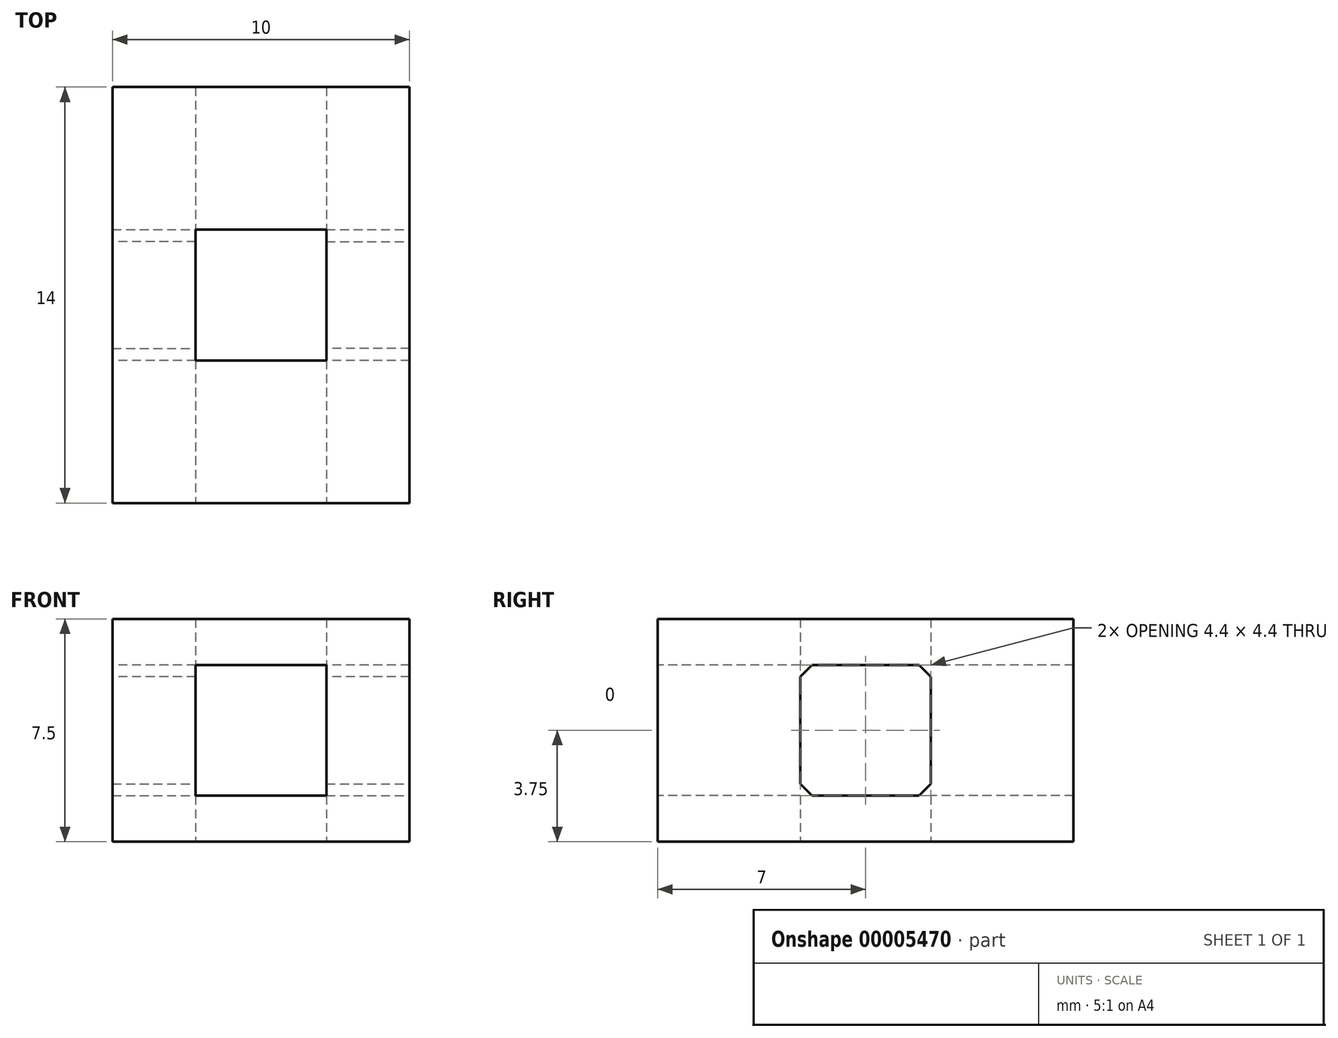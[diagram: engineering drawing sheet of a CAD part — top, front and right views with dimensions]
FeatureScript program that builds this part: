
annotation { "Feature Type Name" : "Feature", "Feature Type Description" : "" }
export const myFeature = defineFeature(function(context is Context, id is Id, definition is map)
    precondition{}
    {
        {
            var Q0;
            Q0=qCreatedBy(makeId("Top.planeOp"),FACE);
            var sketch = newSketch(context, id + "F0", { "sketchPlane" : qUnion([Q0])});
            skLineSegment(sketch, "E0.rect.bottom", {"start": v(5, 7) * mm, "end": v(-5, 7) * mm});
            skLineSegment(sketch, "E0.rect.top", {"start": v(5, -7) * mm, "end": v(-5, -7) * mm});
            skLineSegment(sketch, "E0.rect.left", {"start": v(5, 7) * mm, "end": v(5, -7) * mm});
            skLineSegment(sketch, "E0.rect.right", {"start": v(-5, 7) * mm, "end": v(-5, -7) * mm});
            skPoint(sketch, "E0.rect.middle", {"position": v(0, 0) * mm});
            skLineSegment(sketch, "E1.rect.bottom", {"start": v(2.2, 2.2) * mm, "end": v(-2.2, 2.2) * mm});
            skLineSegment(sketch, "E1.rect.top", {"start": v(2.2, -2.2) * mm, "end": v(-2.2, -2.2) * mm});
            skLineSegment(sketch, "E1.rect.left", {"start": v(2.2, 2.2) * mm, "end": v(2.2, -2.2) * mm});
            skLineSegment(sketch, "E1.rect.right", {"start": v(-2.2, 2.2) * mm, "end": v(-2.2, -2.2) * mm});
            skSolve(sketch);
        }
        {
            var Q0;
            Q0=makeQuery(id+"F0.imprint","IMPRINT",FACE,{"disambiguationData":[TD([[makeQuery(id+"F0.imprint","IMPRINT",EDGE,{"derivedFrom":sQuery(id+"F0.wireOp",EDGE,"E0.rect.bottom")}),1.0]])]});
            extrude(context, id + "F1", {"entities" : qUnion([Q0]), "depth" : 7.5 * mm});
        }
        {
            var Q0;
            Q0=makeQuery(id+"F1.opExtrude","SWEPT_FACE",FACE,{"disambiguationData":[OSD([sQuery(id+"F0.wireOp",EDGE,"E0.rect.right")])]});
            var sketch = newSketch(context, id + "F2", { "sketchPlane" : qUnion([Q0])});
            skLineSegment(sketch, "E2.rect.bottom", {"start": v(-2.2, 5.95) * mm, "end": v(2.2, 5.95) * mm});
            skLineSegment(sketch, "E2.rect.top", {"start": v(-2.2, 1.55) * mm, "end": v(2.2, 1.55) * mm});
            skLineSegment(sketch, "E2.rect.left", {"start": v(-2.2, 5.95) * mm, "end": v(-2.2, 1.55) * mm});
            skLineSegment(sketch, "E2.rect.right", {"start": v(2.2, 5.95) * mm, "end": v(2.2, 1.55) * mm});
            skPoint(sketch, "E2.rect.middle", {"position": v(0, 3.75) * mm});
            skPoint(sketch, "E3", {"position": v(-7, 3.75) * mm});
            skSolve(sketch);
        }
        {
            var Q0;
            Q0=makeQuery(id+"F2.imprint","IMPRINT",FACE,{"disambiguationData":[TD([[makeQuery(id+"F2.imprint","IMPRINT",EDGE,{"derivedFrom":sQuery(id+"F2.wireOp",EDGE,"E2.rect.bottom")}),-1.0]])]});
            extrude(context, id + "F3", {"entities" : qUnion([Q0]), "operationType" : NewBodyOperationType.REMOVE, "endBound" : BoundingType.THROUGH_ALL, "oppositeDirection" : true, "depth" : 25 * mm});
        }
        {
            var Q0;
            Q0=makeQuery(id+"F1.opExtrude","SWEPT_FACE",FACE,{"disambiguationData":[OSD([sQuery(id+"F0.wireOp",EDGE,"E0.rect.top")])]});
            var sketch = newSketch(context, id + "F4", { "sketchPlane" : qUnion([Q0])});
            skLineSegment(sketch, "E4.rect.bottom", {"start": v(2.2, 5.95) * mm, "end": v(-2.2, 5.95) * mm});
            skLineSegment(sketch, "E4.rect.top", {"start": v(2.2, 1.55) * mm, "end": v(-2.2, 1.55) * mm});
            skLineSegment(sketch, "E4.rect.left", {"start": v(2.2, 5.95) * mm, "end": v(2.2, 1.55) * mm});
            skLineSegment(sketch, "E4.rect.right", {"start": v(-2.2, 5.95) * mm, "end": v(-2.2, 1.55) * mm});
            skPoint(sketch, "E4.rect.middle", {"position": v(0, 3.75) * mm});
            skPoint(sketch, "E5", {"position": v(-5, 3.75) * mm});
            skSolve(sketch);
        }
        {
            var Q0;
            Q0=makeQuery(id+"F4.imprint","IMPRINT",FACE,{"disambiguationData":[TD([[makeQuery(id+"F4.imprint","IMPRINT",EDGE,{"derivedFrom":sQuery(id+"F4.wireOp",EDGE,"E4.rect.bottom")}),1.0]])]});
            extrude(context, id + "F5", {"entities" : qUnion([Q0]), "operationType" : NewBodyOperationType.REMOVE, "endBound" : BoundingType.THROUGH_ALL, "oppositeDirection" : true, "depth" : 25 * mm});
        }
        {
            var Q0;
            {var subQ0=sQuery(id+"F2.wireOp",EDGE,"E2.rect.top");var subQ1=sQuery(id+"F2.wireOp",EDGE,"E2.rect.left");Q0=makeQuery(id+"F3.boolean.opBoolean","COPY",EDGE,{"disambiguationData":[TD([makeQuery(id+"F1.opExtrude","SWEPT_FACE",FACE,{"disambiguationData":[OSD([sQuery(id+"F0.wireOp",EDGE,"E0.rect.left")])]})])],"derivedFrom":makeQuery(id+"F3.opExtrude","SWEPT_EDGE",EDGE,{"disambiguationData":[OSD([subQ0,subQ1])]})});}
            var Q1;
            {var subQ0=sQuery(id+"F2.wireOp",EDGE,"E2.rect.bottom");var subQ1=sQuery(id+"F2.wireOp",EDGE,"E2.rect.left");Q1=makeQuery(id+"F3.boolean.opBoolean","COPY",EDGE,{"disambiguationData":[TD([makeQuery(id+"F1.opExtrude","SWEPT_FACE",FACE,{"disambiguationData":[OSD([sQuery(id+"F0.wireOp",EDGE,"E0.rect.left")])]})])],"derivedFrom":makeQuery(id+"F3.opExtrude","SWEPT_EDGE",EDGE,{"disambiguationData":[OSD([subQ0,subQ1])]})});}
            var Q2;
            {var subQ0=sQuery(id+"F2.wireOp",EDGE,"E2.rect.bottom");var subQ1=sQuery(id+"F2.wireOp",EDGE,"E2.rect.right");Q2=makeQuery(id+"F3.boolean.opBoolean","COPY",EDGE,{"disambiguationData":[TD([makeQuery(id+"F1.opExtrude","SWEPT_FACE",FACE,{"disambiguationData":[OSD([sQuery(id+"F0.wireOp",EDGE,"E0.rect.left")])]})])],"derivedFrom":makeQuery(id+"F3.opExtrude","SWEPT_EDGE",EDGE,{"disambiguationData":[OSD([subQ0,subQ1])]})});}
            var Q3;
            {var subQ0=sQuery(id+"F2.wireOp",EDGE,"E2.rect.top");var subQ1=sQuery(id+"F2.wireOp",EDGE,"E2.rect.right");Q3=makeQuery(id+"F3.boolean.opBoolean","COPY",EDGE,{"disambiguationData":[TD([makeQuery(id+"F1.opExtrude","SWEPT_FACE",FACE,{"disambiguationData":[OSD([sQuery(id+"F0.wireOp",EDGE,"E0.rect.left")])]})])],"derivedFrom":makeQuery(id+"F3.opExtrude","SWEPT_EDGE",EDGE,{"disambiguationData":[OSD([subQ0,subQ1])]})});}
            var Q4;
            {var subQ0=sQuery(id+"F2.wireOp",EDGE,"E2.rect.bottom");var subQ1=sQuery(id+"F2.wireOp",EDGE,"E2.rect.right");Q4=makeQuery(id+"F3.boolean.opBoolean","COPY",EDGE,{"disambiguationData":[TD([makeQuery(id+"F1.opExtrude","SWEPT_FACE",FACE,{"disambiguationData":[OSD([sQuery(id+"F0.wireOp",EDGE,"E0.rect.right")])]})])],"derivedFrom":makeQuery(id+"F3.opExtrude","SWEPT_EDGE",EDGE,{"disambiguationData":[OSD([subQ0,subQ1])]})});}
            var Q5;
            {var subQ0=sQuery(id+"F2.wireOp",EDGE,"E2.rect.bottom");var subQ1=sQuery(id+"F2.wireOp",EDGE,"E2.rect.left");Q5=makeQuery(id+"F3.boolean.opBoolean","COPY",EDGE,{"disambiguationData":[TD([makeQuery(id+"F1.opExtrude","SWEPT_FACE",FACE,{"disambiguationData":[OSD([sQuery(id+"F0.wireOp",EDGE,"E0.rect.right")])]})])],"derivedFrom":makeQuery(id+"F3.opExtrude","SWEPT_EDGE",EDGE,{"disambiguationData":[OSD([subQ0,subQ1])]})});}
            var Q6;
            {var subQ0=sQuery(id+"F2.wireOp",EDGE,"E2.rect.top");var subQ1=sQuery(id+"F2.wireOp",EDGE,"E2.rect.left");Q6=makeQuery(id+"F3.boolean.opBoolean","COPY",EDGE,{"disambiguationData":[TD([makeQuery(id+"F1.opExtrude","SWEPT_FACE",FACE,{"disambiguationData":[OSD([sQuery(id+"F0.wireOp",EDGE,"E0.rect.right")])]})])],"derivedFrom":makeQuery(id+"F3.opExtrude","SWEPT_EDGE",EDGE,{"disambiguationData":[OSD([subQ0,subQ1])]})});}
            var Q7;
            {var subQ0=sQuery(id+"F2.wireOp",EDGE,"E2.rect.top");var subQ1=sQuery(id+"F2.wireOp",EDGE,"E2.rect.right");Q7=makeQuery(id+"F3.boolean.opBoolean","COPY",EDGE,{"disambiguationData":[TD([makeQuery(id+"F1.opExtrude","SWEPT_FACE",FACE,{"disambiguationData":[OSD([sQuery(id+"F0.wireOp",EDGE,"E0.rect.right")])]})])],"derivedFrom":makeQuery(id+"F3.opExtrude","SWEPT_EDGE",EDGE,{"disambiguationData":[OSD([subQ0,subQ1])]})});}
            chamfer(context, id + "F6", {"entities" : qUnion([Q0, Q1, Q2, Q3, Q4, Q5, Q6, Q7]), "width" : .4 * mm, "tangentPropagation" : true});
        }
    });
